# Revit family: UNB_Eurovit+_R0267_BIM_NL
name_source: partatom
category: Plumbing Fixtures
units: mm (PartAtom-declared; Revit-internal decimal feet)

## family parameters
Cut with Voids When Loaded = No
Host = Face
Maintain Annotation Orientation = No
OmniClass Number = 23.45.05.14.21.11
OmniClass Title = Bath/Shower Units
Part Type = Normal
Room Calculation Point = No
Round Connector Dimension = Use Diameter
Shared = Yes

## types (4) — shared parameters
Accesoires = https://www.idealstandard.nl
Accessories = https://www.idealstandard.nl
Afmetingen = 1200 x 440 x 550 mm
AfstandsEenheid = millimeter
AreaUnits = millimeter
Assembly Code = C1030200
AssetType = Vast
Auteur = Ideal Standard
BIMObjectName = ISI_IdealStandard_Furniture_R0267
BREEAM = No
BimObjectNaam = ISI_IdealStandard_Furniture_R0267
Brand = Unbranded
Breedte = 1200
ConnectionType = sanitair
CurrencyUnit = €
Default Elevation = 1219 mm
Diepte = 439,999999999982
DurationUnit = jaar
DuurEenheid = jaar
ECA = No
EPD = https://www.idealstandard.nl
ExpectedLife = 30
GemaaktOp = 26/06/2024
Help = https://www.idealstandard.nl
Hoogte = 550,000000000001
Hulp = https://www.idealstandard.nl
IfcExportAs = IfcFurnitureType
Installatieinstructies = https://www.idealstandard.nl
InstallationInstructions = https://www.idealstandard.nl
Lengte = 439,999999999982
LinearUnits = millimeters
Manufacturer = Ideal Standard
ManufacturerURL = https://www.idealstandard.nl
Materiaal = Furniture
Merk = Merkloos
NBSDescription = Baths
Name = ISI_Furniture_Unb_R0267_IdealStandard
NettWeight = Kg
Nettogewicht = Kg
NominalDepth = 440 mm
NominalHeight = 550 mm
NominalLength = 440 mm
NominalWidth = 1200 mm
ProductInformation = https://www.idealstandard.nl
ProductSoort = meubels
Productinformatie = https://www.idealstandard.nl
Shape = Rechthoekig
Size = 1200 x 440 x 550 mm
Space = Intern
SpareParts = https://www.idealstandard.nl
TMV3 = No
Telefoonnummer = 077 355 08 08
Typeconnectie = sanitair
URL = https://www.idealstandard.nl
Uniclass2015Code = Pr_40_20_76
Uniclass2015Title = Sanitary accessories
Uniclass2015Version = Products v1.34
Urlproducent = https://www.idealstandard.nl
ValutaEenheid = €
Versie = 1
Version = 1
VolumeUnits = Liter
Volumeunits = Liter
Vorm = Rechthoekig
WRAS = No
WaarborgGarantieInstallatie = Fabrieksgarantie
WarrantyDescription = Manufacturers Warranty
WarrantyDurationParts = 2
WarrantyDurationUnit = year
WarrantyGuarantorParts = https://www.idealstandard.nl
WaterEfficientProduct = No
Wisselstukken = https://www.idealstandard.nl
zero-valued in all types: Vervangingskosten

## per-type parameters (varying)
| type | Afwerking | Artikelnummer | Artikelomschrijving | BarCode | Color | Description | Eigenschappen | Features | Finish | Kleur | MAT | Model | ModelNumber | ModelReference |
| R0267WG - BASIN UNIT 120x44 4 DWS GLOSSY WHITE | Glanzend wit | R0267WG | Eurovit 2.0 WASTAFEL 120x44 WANDHANGEND 4 LADEN GLANZEND WIT | 3391500589155 | Glanzend wit | Eurovit 2.0 WASTAFEL 120x44 WANDHANGEND 4 LADEN GLANZEND WIT | Eurovit 2.0 WASTAFEL 120x44 WANDHANGEND 4 LADEN GLANZEND WIT | Eurovit 2.0 WASTAFEL 120x44 WANDHANGEND 4 LADEN GLANZEND WIT | Glanzend wit | Glanzend wit | WG-White | R0267WG | R0267WG | Eurovit 2.0 WASTAFEL 120x44 WANDHANGEND 4 LADEN GLANZEND WIT |
| R0267TI - BASIN UNIT 120x44 4 DWS MID GREY | Middengrijs | R0267TI | Eurovit 2.0 WASTAFEL 120x44 WANDHANGEND 4 LADEN MIDDENGRIJS | 3391500589148 | Middengrijs | Eurovit 2.0 WASTAFEL 120x44 WANDHANGEND 4 LADEN MIDDENGRIJS | Eurovit 2.0 WASTAFEL 120x44 WANDHANGEND 4 LADEN MIDDENGRIJS | Eurovit 2.0 WASTAFEL 120x44 WANDHANGEND 4 LADEN MIDDENGRIJS | Middengrijs | Middengrijs | TI | R0267TI | R0267TI | Eurovit 2.0 WASTAFEL 120x44 WANDHANGEND 4 LADEN MIDDENGRIJS |
| R0267Y8 - BASIN UNIT 120x44 4 DWS NATURAL OAK | Natuurlijk eiken | R0267Y8 | Eurovit 2.0 WASTAFEL 120x44 WANDHANGEND 4 LADEN NATUURLIJK EIKEN | 3391500589162 | Natuurlijk eiken | Eurovit 2.0 WASTAFEL 120x44 WANDHANGEND 4 LADEN NATUURLIJK EIKEN | Eurovit 2.0 WASTAFEL 120x44 WANDHANGEND 4 LADEN NATUURLIJK EIKEN | Eurovit 2.0 WASTAFEL 120x44 WANDHANGEND 4 LADEN NATUURLIJK EIKEN | Natuurlijk eiken | Natuurlijk eiken | Y8 | R0267Y8 | R0267Y8 | Eurovit 2.0 WASTAFEL 120x44 WANDHANGEND 4 LADEN NATUURLIJK EIKEN |
| R0267Y9 - BASIN UNIT 120x44 4 DWS FLINT HICKORY | Flint-Hickory | R0267Y9 | Eurovit 2.0 WASTAFEL 120x44 WANDHANGEND 4 LADEN FLINT HICKORY | 3391500589179 | Flint-Hickory | Eurovit 2.0 WASTAFEL 120x44 WANDHANGEND 4 LADEN FLINT HICKORY | Eurovit 2.0 WASTAFEL 120x44 WANDHANGEND 4 LADEN FLINT HICKORY | Eurovit 2.0 WASTAFEL 120x44 WANDHANGEND 4 LADEN FLINT HICKORY | Flint-Hickory | Flint-Hickory | Y9 | R0267Y9 | R0267Y9 | Eurovit 2.0 WASTAFEL 120x44 WANDHANGEND 4 LADEN FLINT HICKORY |

## geometry (parser evidence)
native form markers: Sweep x2
no freeform markers — native parametric forms only
